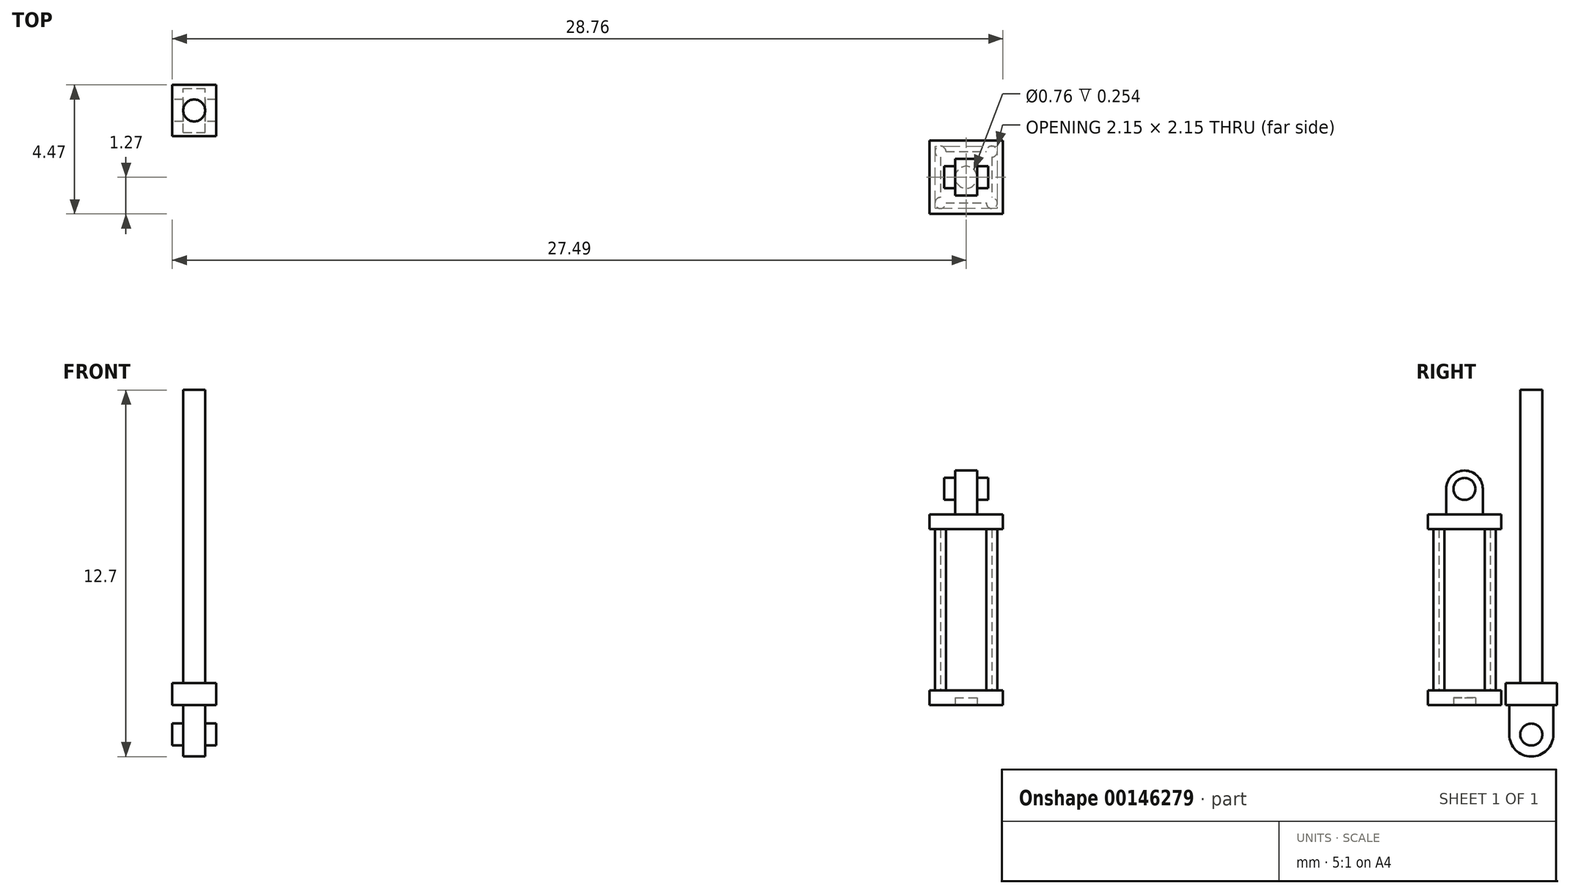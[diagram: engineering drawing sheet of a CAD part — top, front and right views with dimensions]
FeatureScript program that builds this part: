
annotation { "Feature Type Name" : "Feature", "Feature Type Description" : "" }
export const myFeature = defineFeature(function(context is Context, id is Id, definition is map)
    precondition{}
    {
        {
            var Q0;
            Q0=qCreatedBy(makeId("Top.planeOp"),FACE);
            var sketch = newSketch(context, id + "F0", { "sketchPlane" : qUnion([Q0])});
            skLineSegment(sketch, "E0.bottom", {"start": v(0, 0) * mm, "end": v(-2.54, 0) * mm});
            skLineSegment(sketch, "E0.top", {"start": v(0, 2.54) * mm, "end": v(-2.54, 2.54) * mm});
            skLineSegment(sketch, "E0.left", {"start": v(0, 0) * mm, "end": v(0, 2.54) * mm});
            skLineSegment(sketch, "E0.right", {"start": v(-2.54, 0) * mm, "end": v(-2.54, 2.54) * mm});
            skSolve(sketch);
        }
        {
            var Q0;
            Q0=makeQuery(id+"F0.imprint","IMPRINT",FACE,{"disambiguationData":[TD([[makeQuery(id+"F0.imprint","IMPRINT",EDGE,{"derivedFrom":sQuery(id+"F0.wireOp",EDGE,"E0.bottom")}),-1.0]])]});
            extrude(context, id + "F1", {"entities" : qUnion([Q0]), "depth" : 0.5 * mm});
        }
        {
            var Q0;
            Q0=makeQuery(id+"F1.opExtrude","CAP_FACE",FACE,{"disambiguationData":[OSD([sQuery(id+"F0.wireOp",EDGE,"E0.bottom"),sQuery(id+"F0.wireOp",EDGE,"E0.top"),sQuery(id+"F0.wireOp",EDGE,"E0.left"),sQuery(id+"F0.wireOp",EDGE,"E0.right")])],"isStart":false});
            var sketch = newSketch(context, id + "F2", { "sketchPlane" : qUnion([Q0])});
            skLineSegment(sketch, "E1.bottom", {"start": v(-2.16, 2.16) * mm, "end": v(-0.38, 2.16) * mm});
            skLineSegment(sketch, "E1.top", {"start": v(-2.16, 0.38) * mm, "end": v(-0.38, 0.38) * mm});
            skLineSegment(sketch, "E1.left", {"start": v(-2.16, 2.16) * mm, "end": v(-2.16, 0.38) * mm});
            skLineSegment(sketch, "E1.right", {"start": v(-0.38, 2.16) * mm, "end": v(-0.38, 0.38) * mm});
            skSolve(sketch);
        }
        {
            var Q0;
            Q0=makeQuery(id+"F1.opExtrude","CAP_FACE",FACE,{"disambiguationData":[OSD([sQuery(id+"F0.wireOp",EDGE,"E0.bottom"),sQuery(id+"F0.wireOp",EDGE,"E0.top"),sQuery(id+"F0.wireOp",EDGE,"E0.left"),sQuery(id+"F0.wireOp",EDGE,"E0.right")])],"isStart":false});
            var sketch = newSketch(context, id + "F3", { "sketchPlane" : qUnion([Q0])});
            skCircle(sketch, "E2", {"center": v(-2.16, 0.38) * mm, "radius": 0.2 * mm});
            skCircle(sketch, "E3", {"center": v(-0.38, 0.38) * mm, "radius": 0.2 * mm});
            skCircle(sketch, "E4", {"center": v(-0.38, 2.16) * mm, "radius": 0.2 * mm});
            skCircle(sketch, "E5", {"center": v(-2.16, 2.16) * mm, "radius": 0.2 * mm});
            skSolve(sketch);
        }
        {
            var Q0;
            Q0 = qSketchRegion(id + "F3", true);
            var Q1;
            Q1=makeQuery(id+"F2.imprint","IMPRINT",FACE,{"disambiguationData":[TD([[makeQuery(id+"F2.imprint","IMPRINT",EDGE,{"derivedFrom":sQuery(id+"F2.wireOp",EDGE,"E1.bottom")}),-1.0]])]});
            extrude(context, id + "F4", {"entities" : qUnion([Q0, Q1]), "operationType" : NewBodyOperationType.ADD, "depth" : 5.6 * mm});
        }
        {
            var Q0;
            Q0=makeQuery(id+"F4.boolean.opBoolean","MERGE",FACE,{"derivedFrom":[makeQuery(id+"F4.opExtrude","CAP_FACE",FACE,{"disambiguationData":[OSD([sQuery(id+"F2.wireOp",EDGE,"E1.bottom"),sQuery(id+"F2.wireOp",EDGE,"E1.top"),sQuery(id+"F2.wireOp",EDGE,"E1.left"),sQuery(id+"F2.wireOp",EDGE,"E1.right")])],"isStart":false}),makeQuery(id+"F4.opExtrude","CAP_FACE",FACE,{"disambiguationData":[OSD([sQuery(id+"F3.wireOp",EDGE,"E2")])],"isStart":false}),makeQuery(id+"F4.opExtrude","CAP_FACE",FACE,{"disambiguationData":[OSD([sQuery(id+"F3.wireOp",EDGE,"E3")])],"isStart":false}),makeQuery(id+"F4.opExtrude","CAP_FACE",FACE,{"disambiguationData":[OSD([sQuery(id+"F3.wireOp",EDGE,"E4")])],"isStart":false}),makeQuery(id+"F4.opExtrude","CAP_FACE",FACE,{"disambiguationData":[OSD([sQuery(id+"F3.wireOp",EDGE,"E5")])],"isStart":false})]});
            var sketch = newSketch(context, id + "F5", { "sketchPlane" : qUnion([Q0])});
            skLineSegment(sketch, "E6.bottom", {"start": v(0, 0) * mm, "end": v(-2.54, 0) * mm});
            skLineSegment(sketch, "E6.top", {"start": v(0, 2.54) * mm, "end": v(-2.54, 2.54) * mm});
            skLineSegment(sketch, "E6.left", {"start": v(0, 0) * mm, "end": v(0, 2.54) * mm});
            skLineSegment(sketch, "E6.right", {"start": v(-2.54, 0) * mm, "end": v(-2.54, 2.54) * mm});
            skSolve(sketch);
        }
        {
            var Q0;
            Q0 = qSketchRegion(id + "F5", true);
            extrude(context, id + "F6", {"entities" : qUnion([Q0]), "operationType" : NewBodyOperationType.ADD, "depth" : 0.5 * mm});
        }
        {
            var Q0;
            Q0=makeQuery(id+"F6.opExtrude","CAP_FACE",FACE,{"disambiguationData":[OSD([sQuery(id+"F5.wireOp",EDGE,"E6.bottom"),sQuery(id+"F5.wireOp",EDGE,"E6.top"),sQuery(id+"F5.wireOp",EDGE,"E6.left"),sQuery(id+"F5.wireOp",EDGE,"E6.right")])],"isStart":false});
            var sketch = newSketch(context, id + "F7", { "sketchPlane" : qUnion([Q0])});
            skLineSegment(sketch, "E7.bottom", {"start": v(-1.65, 1.9) * mm, "end": v(-0.89, 1.9) * mm});
            skLineSegment(sketch, "E7.top", {"start": v(-1.65, 0.64) * mm, "end": v(-0.89, 0.64) * mm});
            skLineSegment(sketch, "E7.left", {"start": v(-1.65, 1.9) * mm, "end": v(-1.65, 0.63) * mm});
            skLineSegment(sketch, "E7.right", {"start": v(-0.89, 1.9) * mm, "end": v(-0.89, 0.64) * mm});
            skSolve(sketch);
        }
        {
            var Q0;
            Q0=makeQuery(id+"F7.imprint","IMPRINT",FACE,{"disambiguationData":[TD([[makeQuery(id+"F7.imprint","IMPRINT",EDGE,{"derivedFrom":sQuery(id+"F7.wireOp",EDGE,"E7.bottom")}),-1.0]])]});
            extrude(context, id + "F8", {"entities" : qUnion([Q0]), "operationType" : NewBodyOperationType.ADD, "depth" : 1.52 * mm});
        }
        {
            var Q0;
            Q0=makeQuery(id+"F8.opExtrude","CAP_EDGE",EDGE,{"disambiguationData":[OSD([sQuery(id+"F7.wireOp",EDGE,"SnMZz6UM-2eJR-UkkT-urh7-qXkrGxYPXZd4.bottom")])],"isStart":false});
            var Q1;
            Q1=makeQuery(id+"F8.opExtrude","CAP_EDGE",EDGE,{"disambiguationData":[OSD([sQuery(id+"F7.wireOp",EDGE,"SnMZz6UM-2eJR-UkkT-urh7-qXkrGxYPXZd4.top")])],"isStart":false});
            var Q2;
            Q2=makeQuery(id+"F8.opExtrude","CAP_EDGE",EDGE,{"disambiguationData":[OSD([sQuery(id+"F7.wireOp",EDGE,"E7.top")])],"isStart":false});
            var Q3;
            Q3=makeQuery(id+"F8.opExtrude","CAP_EDGE",EDGE,{"disambiguationData":[OSD([sQuery(id+"F7.wireOp",EDGE,"E7.bottom")])],"isStart":false});
            fillet(context, id + "F9", {"entities" : qUnion([Q0, Q1, Q2, Q3]), "radius" : 0.64 * mm, "tangentPropagation" : true, "allowEdgeOverflow" : false});
        }
        {
            var Q0;
            Q0=makeQuery(id+"F1.opExtrude","CAP_FACE",FACE,{"disambiguationData":[OSD([sQuery(id+"F0.wireOp",EDGE,"E0.bottom"),sQuery(id+"F0.wireOp",EDGE,"E0.top"),sQuery(id+"F0.wireOp",EDGE,"E0.left"),sQuery(id+"F0.wireOp",EDGE,"E0.right")])],"isStart":true});
            var sketch = newSketch(context, id + "F10", { "sketchPlane" : qUnion([Q0])});
            skCircle(sketch, "E8", {"center": v(-1.27, -1.27) * mm, "radius": 0.38 * mm});
            skPoint(sketch, "E8.centerSnap0", {"position": v(-1.27, -2.54) * mm});
            skPoint(sketch, "E8.centerSnap1", {"position": v(-2.54, -1.27) * mm});
            skSolve(sketch);
        }
        {
            var Q0;
            Q0 = qSketchRegion(id + "F10", true);
            extrude(context, id + "F11", {"entities" : qUnion([Q0]), "operationType" : NewBodyOperationType.REMOVE, "oppositeDirection" : true, "depth" : 0.25 * mm});
        }
        {
            var Q0;
            Q0=qCreatedBy(makeId("Top.planeOp"),FACE);
            var sketch = newSketch(context, id + "F12", { "sketchPlane" : qUnion([Q0])});
            skLineSegment(sketch, "E9.bottom", {"start": v(-28.76, 4.47) * mm, "end": v(-27.24, 4.47) * mm});
            skLineSegment(sketch, "E9.top", {"start": v(-28.76, 2.7) * mm, "end": v(-27.24, 2.7) * mm});
            skLineSegment(sketch, "E9.left", {"start": v(-28.76, 4.47) * mm, "end": v(-28.76, 2.7) * mm});
            skLineSegment(sketch, "E9.right", {"start": v(-27.24, 4.47) * mm, "end": v(-27.24, 2.7) * mm});
            skSolve(sketch);
        }
        {
            var Q0;
            Q0 = qSketchRegion(id + "F12", true);
            extrude(context, id + "F13", {"entities" : qUnion([Q0]), "depth" : 0.76 * mm});
        }
        {
            var Q0;
            Q0=makeQuery(id+"F13.opExtrude","CAP_FACE",FACE,{"disambiguationData":[OSD([sQuery(id+"F12.wireOp",EDGE,"E9.bottom"),sQuery(id+"F12.wireOp",EDGE,"E9.top"),sQuery(id+"F12.wireOp",EDGE,"E9.left"),sQuery(id+"F12.wireOp",EDGE,"E9.right")])],"isStart":false});
            var sketch = newSketch(context, id + "F14", { "sketchPlane" : qUnion([Q0])});
            skCircle(sketch, "E10", {"center": v(-28, 3.59) * mm, "radius": 0.38 * mm});
            skPoint(sketch, "E10.centerSnap0", {"position": v(-28.76, 3.59) * mm});
            skPoint(sketch, "E10.centerSnap1", {"position": v(-28, 4.47) * mm});
            skSolve(sketch);
        }
        {
            var Q0;
            Q0 = qSketchRegion(id + "F14", true);
            extrude(context, id + "F15", {"entities" : qUnion([Q0]), "operationType" : NewBodyOperationType.ADD, "depth" : 10.16 * mm});
        }
        {
            var Q0;
            Q0=makeQuery(id+"F13.opExtrude","CAP_FACE",FACE,{"disambiguationData":[OSD([sQuery(id+"F12.wireOp",EDGE,"E9.bottom"),sQuery(id+"F12.wireOp",EDGE,"E9.top"),sQuery(id+"F12.wireOp",EDGE,"E9.left"),sQuery(id+"F12.wireOp",EDGE,"E9.right")])],"isStart":true});
            var sketch = newSketch(context, id + "F16", { "sketchPlane" : qUnion([Q0])});
            skLineSegment(sketch, "E11.bottom", {"start": v(-28.38, -2.82) * mm, "end": v(-27.62, -2.82) * mm});
            skLineSegment(sketch, "E11.top", {"start": v(-28.38, -4.35) * mm, "end": v(-27.62, -4.35) * mm});
            skLineSegment(sketch, "E11.left", {"start": v(-28.38, -2.82) * mm, "end": v(-28.38, -4.35) * mm});
            skLineSegment(sketch, "E11.right", {"start": v(-27.62, -2.82) * mm, "end": v(-27.62, -4.35) * mm});
            skSolve(sketch);
        }
        {
            var Q0;
            Q0 = qSketchRegion(id + "F16", true);
            extrude(context, id + "F17", {"entities" : qUnion([Q0]), "operationType" : NewBodyOperationType.ADD, "depth" : 1.78 * mm});
        }
        {
            var Q0;
            Q0=makeQuery(id+"F17.opExtrude","CAP_EDGE",EDGE,{"disambiguationData":[OSD([sQuery(id+"F16.wireOp",EDGE,"E11.bottom")])],"isStart":false});
            var Q1;
            Q1=makeQuery(id+"F17.opExtrude","CAP_EDGE",EDGE,{"disambiguationData":[OSD([sQuery(id+"F16.wireOp",EDGE,"E11.top")])],"isStart":false});
            var Q2;
            Q2=makeQuery(id+"F17.opExtrude","CAP_EDGE",EDGE,{"disambiguationData":[OSD([sQuery(id+"F16.wireOp",EDGE,"ZLugjXCQ-A49h-u4Kn-CDT1-VXdTF1MAhCxP.top")])],"isStart":false});
            var Q3;
            Q3=makeQuery(id+"F17.opExtrude","CAP_EDGE",EDGE,{"disambiguationData":[OSD([sQuery(id+"F16.wireOp",EDGE,"ZLugjXCQ-A49h-u4Kn-CDT1-VXdTF1MAhCxP.bottom")])],"isStart":false});
            fillet(context, id + "F18", {"entities" : qUnion([Q0, Q1, Q2, Q3]), "radius" : 0.76 * mm, "tangentPropagation" : true, "allowEdgeOverflow" : false});
        }
        {
            var Q0;
            Q0=makeQuery(id+"F8.opExtrude","SWEPT_FACE",FACE,{"disambiguationData":[OSD([sQuery(id+"F7.wireOp",EDGE,"E7.right")])]});
            var sketch = newSketch(context, id + "F19", { "sketchPlane" : qUnion([Q0])});
            skCircle(sketch, "E12", {"center": v(1.27, 7.5) * mm, "radius": 0.38 * mm});
            skSolve(sketch);
        }
        {
            var Q0;
            Q0 = qSketchRegion(id + "F19", true);
            extrude(context, id + "F20", {"entities" : qUnion([Q0]), "operationType" : NewBodyOperationType.ADD, "depth" : 0.38 * mm, "hasSecondDirection" : true, "secondDirectionOppositeDirection" : true, "secondDirectionDepth" : 1.14 * mm});
        }
        {
            var Q0;
            Q0=makeQuery(id+"F17.opExtrude","SWEPT_FACE",FACE,{"disambiguationData":[OSD([sQuery(id+"F16.wireOp",EDGE,"E11.right")])]});
            var sketch = newSketch(context, id + "F21", { "sketchPlane" : qUnion([Q0])});
            skCircle(sketch, "E13", {"center": v(3.59, -1.02) * mm, "radius": 0.38 * mm});
            skSolve(sketch);
        }
        {
            var Q0;
            Q0 = qSketchRegion(id + "F21", true);
            extrude(context, id + "F22", {"entities" : qUnion([Q0]), "operationType" : NewBodyOperationType.ADD, "depth" : 0.38 * mm, "hasSecondDirection" : true, "secondDirectionOppositeDirection" : true, "secondDirectionDepth" : 1.14 * mm});
        }
    });
